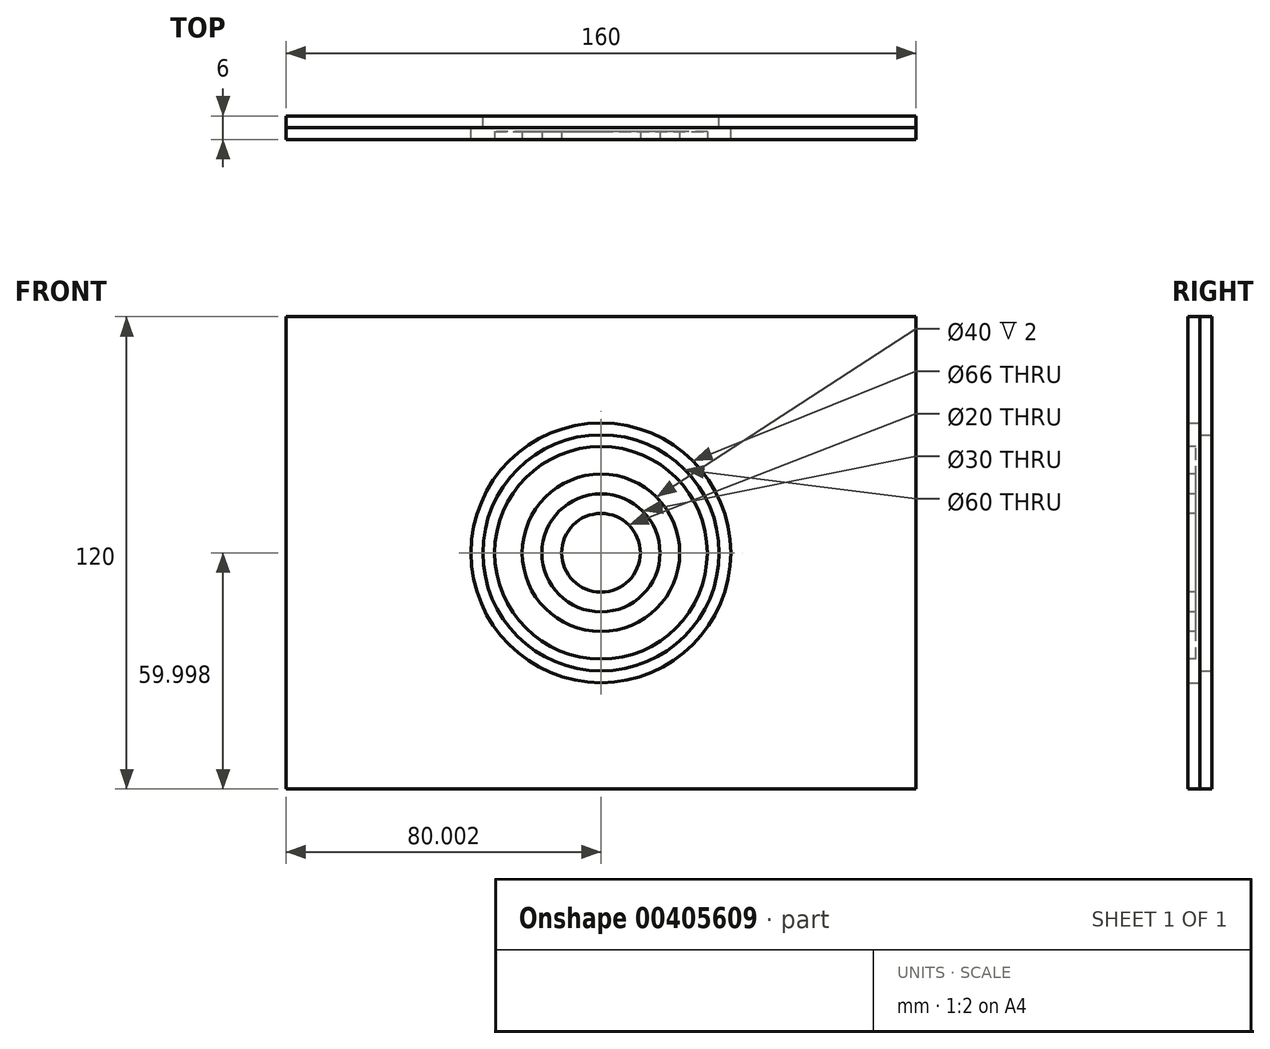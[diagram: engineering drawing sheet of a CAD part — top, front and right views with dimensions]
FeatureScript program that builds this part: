
annotation { "Feature Type Name" : "Feature", "Feature Type Description" : "" }
export const myFeature = defineFeature(function(context is Context, id is Id, definition is map)
    precondition{}
    {
        {
            var Q0;
            Q0=qCreatedBy(makeId("Front.planeOp"),FACE);
            var sketch = newSketch(context, id + "F0", { "sketchPlane" : qUnion([Q0])});
            skLineSegment(sketch, "E0.bottom", {"start": v(-52.38, 81.95) * mm, "end": v(107.62, 81.95) * mm});
            skLineSegment(sketch, "E0.top", {"start": v(-52.38, -38.05) * mm, "end": v(107.62, -38.05) * mm});
            skLineSegment(sketch, "E0.left", {"start": v(-52.38, 81.95) * mm, "end": v(-52.38, -38.05) * mm});
            skLineSegment(sketch, "E0.right", {"start": v(107.62, 81.95) * mm, "end": v(107.62, -38.05) * mm});
            skLineSegment(sketch, "E1", {"start": v(-52.38, 21.95) * mm, "end": v(107.62, 21.95) * mm, "construction": true});
            skLineSegment(sketch, "E2", {"start": v(27.62, 81.95) * mm, "end": v(27.62, -38.05) * mm, "construction": true});
            skCircle(sketch, "E3", {"center": v(27.62, 21.95) * mm, "radius": 30 * mm});
            skSolve(sketch);
        }
        {
            var Q0;
            Q0 = qSketchRegion(id + "F0", true);
            extrude(context, id + "F1", {"entities" : qUnion([Q0]), "depth" : 3 * mm});
        }
        {
            var Q0;
            Q0=makeQuery(id+"F1.opExtrude","CAP_FACE",FACE,{"disambiguationData":[OSD([sQuery(id+"F0.wireOp",EDGE,"E0.bottom"),sQuery(id+"F0.wireOp",EDGE,"E0.top"),sQuery(id+"F0.wireOp",EDGE,"E0.left"),sQuery(id+"F0.wireOp",EDGE,"E0.right"),sQuery(id+"F0.wireOp",EDGE,"E3")])],"isStart":false});
            var sketch = newSketch(context, id + "F2", { "sketchPlane" : qUnion([Q0])});
            skLineSegment(sketch, "E4.bottom", {"start": v(-52.38, 81.95) * mm, "end": v(107.62, 81.95) * mm});
            skLineSegment(sketch, "E4.top", {"start": v(-52.38, -38.05) * mm, "end": v(107.62, -38.05) * mm});
            skLineSegment(sketch, "E4.left", {"start": v(-52.38, 81.95) * mm, "end": v(-52.38, -38.05) * mm});
            skLineSegment(sketch, "E4.right", {"start": v(107.62, 81.95) * mm, "end": v(107.62, -38.05) * mm});
            skCircle(sketch, "E5", {"center": v(27.62, 21.95) * mm, "radius": 33 * mm});
            skSolve(sketch);
        }
        {
            var Q0;
            Q0 = qSketchRegion(id + "F2", true);
            extrude(context, id + "F3", {"entities" : qUnion([Q0]), "depth" : 3 * mm});
        }
        {
            var Q0;
            Q0=makeQuery(id+"F3.opExtrude","CAP_FACE",FACE,{"disambiguationData":[OSD([sQuery(id+"F2.wireOp",EDGE,"E4.bottom"),sQuery(id+"F2.wireOp",EDGE,"E4.top"),sQuery(id+"F2.wireOp",EDGE,"E4.left"),sQuery(id+"F2.wireOp",EDGE,"E4.right"),sQuery(id+"F2.wireOp",EDGE,"E5")])],"isStart":false});
            var sketch = newSketch(context, id + "F4", { "sketchPlane" : qUnion([Q0])});
            skCircle(sketch, "E6", {"center": v(27.62, 21.95) * mm, "radius": 27 * mm});
            skCircle(sketch, "E7", {"center": v(27.62, 21.95) * mm, "radius": 20 * mm});
            skSolve(sketch);
        }
        {
            var Q0;
            Q0 = qSketchRegion(id + "F4", true);
            extrude(context, id + "F5", {"entities" : qUnion([Q0]), "oppositeDirection" : true, "depth" : 2 * mm});
        }
        {
            var Q0;
            Q0=makeQuery(id+"F3.opExtrude","CAP_FACE",FACE,{"disambiguationData":[OSD([sQuery(id+"F2.wireOp",EDGE,"E4.bottom"),sQuery(id+"F2.wireOp",EDGE,"E4.top"),sQuery(id+"F2.wireOp",EDGE,"E4.left"),sQuery(id+"F2.wireOp",EDGE,"E4.right"),sQuery(id+"F2.wireOp",EDGE,"E5")])],"isStart":false});
            var sketch = newSketch(context, id + "F6", { "sketchPlane" : qUnion([Q0])});
            skCircle(sketch, "E8", {"center": v(27.62, 21.95) * mm, "radius": 27 * mm});
            skCircle(sketch, "E9", {"center": v(27.62, 21.95) * mm, "radius": 15 * mm});
            skSolve(sketch);
        }
        {
            var Q0;
            Q0 = qSketchRegion(id + "F6", true);
            extrude(context, id + "F7", {"entities" : qUnion([Q0]), "oppositeDirection" : true, "depth" : 2 * mm});
        }
        {
            var Q0;
            Q0=makeQuery(id+"F3.opExtrude","CAP_FACE",FACE,{"disambiguationData":[OSD([sQuery(id+"F2.wireOp",EDGE,"E4.bottom"),sQuery(id+"F2.wireOp",EDGE,"E4.top"),sQuery(id+"F2.wireOp",EDGE,"E4.left"),sQuery(id+"F2.wireOp",EDGE,"E4.right"),sQuery(id+"F2.wireOp",EDGE,"E5")])],"isStart":false});
            var sketch = newSketch(context, id + "F8", { "sketchPlane" : qUnion([Q0])});
            skCircle(sketch, "E10", {"center": v(27.62, 21.95) * mm, "radius": 27 * mm});
            skCircle(sketch, "E11", {"center": v(27.62, 21.95) * mm, "radius": 10 * mm});
            skSolve(sketch);
        }
        {
            var Q0;
            Q0 = qSketchRegion(id + "F8", true);
            extrude(context, id + "F9", {"entities" : qUnion([Q0]), "oppositeDirection" : true, "depth" : 2 * mm});
        }
    });
